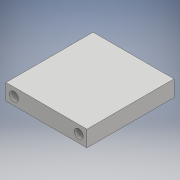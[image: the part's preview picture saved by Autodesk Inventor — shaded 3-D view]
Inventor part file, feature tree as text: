
AUTODESK INVENTOR PART (.ipt)
format: ipt  version: 2017 (Build 210142000, 142)  size: 206,848 bytes
history: native  units: mm
features: extrude x2, sketch x2
ambient origin geometry x8: Origin, YZ Plane, XZ Plane, XY Plane, X Axis, Y Axis, Z Axis, Center Point
bodies: Solide1 (feature_tree)
feature tree (4):
  extrude  "Extrusion1"  Depth=50.0mm
  extrude  "Extrusion2"  Depth=10.0mm
  sketch  "Esquisse1"
  sketch  "Esquisse2"
